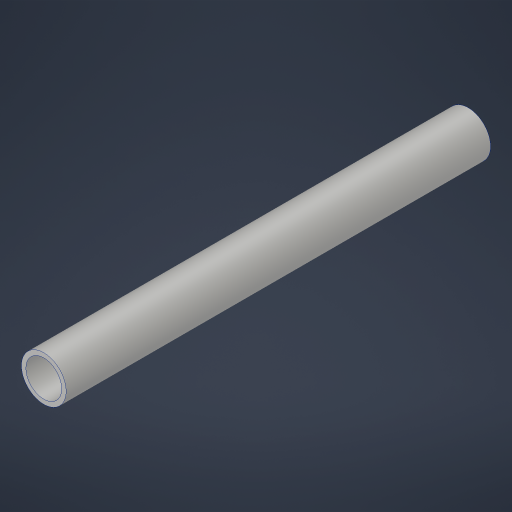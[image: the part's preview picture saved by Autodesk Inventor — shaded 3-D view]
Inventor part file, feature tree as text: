
AUTODESK INVENTOR PART (.ipt)
format: ipt  version: 2023.4 (Build 274418000, 418)  size: 168,448 bytes
history: native  units: in
note: dims shown in document units (in); Inventor stores cm internally (conversion verified against a paired STEP export)
features: extrude x1, sketch x1
ambient origin geometry x8: Origin, YZ Plane, XZ Plane, XY Plane, X Axis, Y Axis, Z Axis, Center Point
bodies: Solid1 (feature_tree)
feature tree (2):
  extrude  "Extrusion1"  Depth=11.875in
  sketch  "Sketch1"  dims[d0=1.25in d1=0.125in d2=11.875in d3=0.0in]
